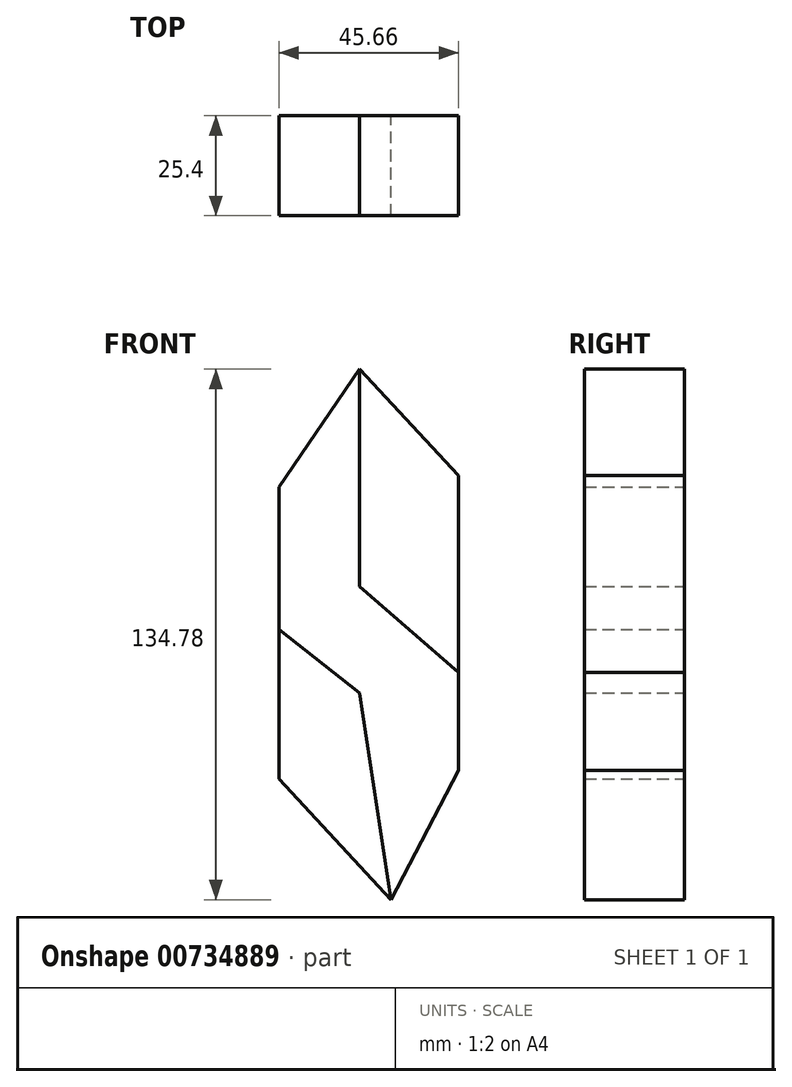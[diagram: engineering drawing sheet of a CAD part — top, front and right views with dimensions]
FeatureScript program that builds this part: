
annotation { "Feature Type Name" : "Feature", "Feature Type Description" : "" }
export const myFeature = defineFeature(function(context is Context, id is Id, definition is map)
    precondition{}
    {
        {
            var Q0;
            Q0=qCreatedBy(makeId("Front.planeOp"),FACE);
            var sketch = newSketch(context, id + "F0", { "sketchPlane" : qUnion([Q0])});
            skCircle(sketch, "E0", {"center": v(-120.56, 24.27) * mm, "radius": 17.21 * mm});
            skLineSegment(sketch, "E1", {"start": v(-109.4, 37.38) * mm, "end": v(-105.87, 163.6) * mm});
            skLineSegment(sketch, "E2", {"start": v(-128.38, 39.6) * mm, "end": v(-123.75, 161.15) * mm});
            skCircle(sketch, "E3", {"center": v(-115.63, 161.33) * mm, "radius": 19.8 * mm});
            skSolve(sketch);
        }
        {
            var Q0;
            Q0 = qSketchRegion(id + "F0", true);
            extrude(context, id + "F1", {"entities" : qUnion([Q0]), "depth" : 25.4 * mm, "offsetDistance" : 25.4 * mm});
        }
        {
            var Q0;
            Q0=qCreatedBy(makeId("Front.planeOp"),FACE);
            var sketch = newSketch(context, id + "F2", { "sketchPlane" : qUnion([Q0])});
            skCircle(sketch, "E4", {"center": v(-119.41, 24.94) * mm, "radius": 5.31 * mm});
            skSolve(sketch);
        }
        {
            var Q0;
            Q0=sQuery(id+"F2.wireOp",VERTEX,"E4.center");
            var Q1;
            Q1=makeQuery(id+"F1.opExtrude","SWEPT_BODY",BODY,{"disambiguationData":[OSD([sQuery(id+"F0.wireOp",EDGE,"E0"),sQuery(id+"F0.wireOp",EDGE,"E1"),sQuery(id+"F0.wireOp",EDGE,"E2"),sQuery(id+"F0.wireOp",EDGE,"E3")])]});
            hole(context, id + "F3", {"style" : HoleStyle.SIMPLE, "endStyle" : HoleEndStyle.THROUGH, "oppositeDirection" : true, "holeDiameter" : 6.35 * mm, "majorDiameter" : 6.35 * mm, "isTappedThrough" : true, "tappedDepth" : 12.7 * mm, "tapClearance" : 3, "locations" : qUnion([Q0]), "scope" : qUnion([Q1])});
        }
        {
            var Q0;
            Q0=qCreatedBy(makeId("Front.planeOp"),FACE);
            var sketch = newSketch(context, id + "F4", { "sketchPlane" : qUnion([Q0])});
            skCircle(sketch, "E5", {"center": v(-114.64, 176.65) * mm, "radius": 15.08 * mm});
            skPoint(sketch, "E5.first.point", {"position": v(-112.92, 161.66) * mm});
            skPoint(sketch, "E5.second.point", {"position": v(-117.3, 191.49) * mm});
            skPoint(sketch, "E5.third.point", {"position": v(-100.26, 181.18) * mm});
            skSolve(sketch);
        }
        {
            var Q0;
            Q0=sQuery(id+"F4.wireOp",VERTEX,"E5.center");
            var Q1;
            Q1=makeQuery(id+"F1.opExtrude","SWEPT_BODY",BODY,{"disambiguationData":[OSD([sQuery(id+"F0.wireOp",EDGE,"E0"),sQuery(id+"F0.wireOp",EDGE,"E1"),sQuery(id+"F0.wireOp",EDGE,"E2"),sQuery(id+"F0.wireOp",EDGE,"E3")])]});
            hole(context, id + "F5", {"style" : HoleStyle.SIMPLE, "endStyle" : HoleEndStyle.THROUGH, "oppositeDirection" : true, "holeDiameter" : 6.35 * mm, "majorDiameter" : 6.35 * mm, "isTappedThrough" : true, "tappedDepth" : 12.7 * mm, "tapClearance" : 3, "locations" : qUnion([Q0]), "scope" : qUnion([Q1])});
        }
        {
            var Q0;
            Q0=makeQuery(id+"F1.opExtrude","SWEPT_BODY",BODY,{"disambiguationData":[OSD([sQuery(id+"F0.wireOp",EDGE,"E0"),sQuery(id+"F0.wireOp",EDGE,"E1"),sQuery(id+"F0.wireOp",EDGE,"E2"),sQuery(id+"F0.wireOp",EDGE,"E3")])]});
            deleteBodies(context, id + "F6", {"entities" : qUnion([Q0])});
        }
        {
            var Q0;
            Q0=qCreatedBy(makeId("Front.planeOp"),FACE);
            var sketch = newSketch(context, id + "F7", { "sketchPlane" : qUnion([Q0])});
            skLineSegment(sketch, "E6", {"start": v(-39.63, 66.11) * mm, "end": v(-14.43, 39.08) * mm});
            skLineSegment(sketch, "E7", {"start": v(-14.43, 39.08) * mm, "end": v(-14.43, 13.88) * mm});
            skLineSegment(sketch, "E8", {"start": v(-14.43, 13.88) * mm, "end": v(-14.43, -35.8) * mm});
            skLineSegment(sketch, "E9", {"start": v(-14.43, -35.8) * mm, "end": v(-31.6, -68.67) * mm});
            skLineSegment(sketch, "E10", {"start": v(-31.6, -68.67) * mm, "end": v(-60.09, -37.99) * mm});
            skLineSegment(sketch, "E11", {"start": v(-60.09, -37.99) * mm, "end": v(-60.09, 36.16) * mm});
            skLineSegment(sketch, "E12", {"start": v(-60.09, 36.16) * mm, "end": v(-39.63, 66.11) * mm});
            skLineSegment(sketch, "E13", {"start": v(-60.09, 0) * mm, "end": v(-39.63, -16.07) * mm});
            skLineSegment(sketch, "E14", {"start": v(-39.63, -16.07) * mm, "end": v(-31.6, -68.67) * mm});
            skLineSegment(sketch, "E15", {"start": v(-39.63, 66.11) * mm, "end": v(-39.63, 10.96) * mm});
            skLineSegment(sketch, "E16", {"start": v(-39.63, 10.96) * mm, "end": v(-14.43, -10.96) * mm});
            skSolve(sketch);
        }
        {
            var Q0;
            {var subQ3=sQuery(id+"F7.wireOp",EDGE,"E9");Q0=makeQuery(id+"F7.imprint","IMPRINT",FACE,{"disambiguationData":[TD([[makeQuery(id+"F7.imprint","IMPRINT",EDGE,{"derivedFrom":subQ3}),-1.0]])]});}
            var sketch = newSketch(context, id + "F8", { "sketchPlane" : qUnion([Q0])});
            skLineSegment(sketch, "E17", {"start": v(-39.09, 66.27) * mm, "end": v(-39.09, 93.76) * mm});
            skLineSegment(sketch, "E18", {"start": v(-39.09, 93.76) * mm, "end": v(-60.78, 60.44) * mm});
            skLineSegment(sketch, "E19", {"start": v(-60.78, 60.44) * mm, "end": v(-60.78, 35.71) * mm});
            skLineSegment(sketch, "E20", {"start": v(-39.09, 93.76) * mm, "end": v(-15.48, 65.6) * mm});
            skLineSegment(sketch, "E21", {"start": v(-15.48, 65.6) * mm, "end": v(-15.48, 39.07) * mm});
            skSolve(sketch);
        }
        {
            var Q0;
            Q0 = qSketchRegion(id + "F8", true);
            var Q1;
            {var subQ3=sQuery(id+"F7.wireOp",EDGE,"E9");Q1=makeQuery(id+"F8.imprint","IMPRINT",FACE,{"disambiguationData":[TD([[makeQuery(id+"F8.imprint","IMPRINT",EDGE,{"derivedFrom":makeQuery(id+"F7.imprint","IMPRINT",EDGE,{"derivedFrom":subQ3})}),-1.0]])]});}
            var Q2;
            Q2=makeQuery(id+"F7.imprint","IMPRINT",FACE,{"disambiguationData":[TD([[makeQuery(id+"F7.imprint","IMPRINT",EDGE,{"derivedFrom":sQuery(id+"F7.wireOp",EDGE,"E6")}),-1.0]])]});
            var Q3;
            {var subQ0=sQuery(id+"F7.wireOp",EDGE,"E10");Q3=makeQuery(id+"F7.imprint","IMPRINT",FACE,{"disambiguationData":[TD([[makeQuery(id+"F7.imprint","IMPRINT",EDGE,{"derivedFrom":subQ0}),-1.0]])]});}
            extrude(context, id + "F9", {"entities" : qUnion([Q0, Q1, Q2, Q3]), "depth" : 25.4 * mm, "offsetDistance" : 25.4 * mm});
        }
    });
